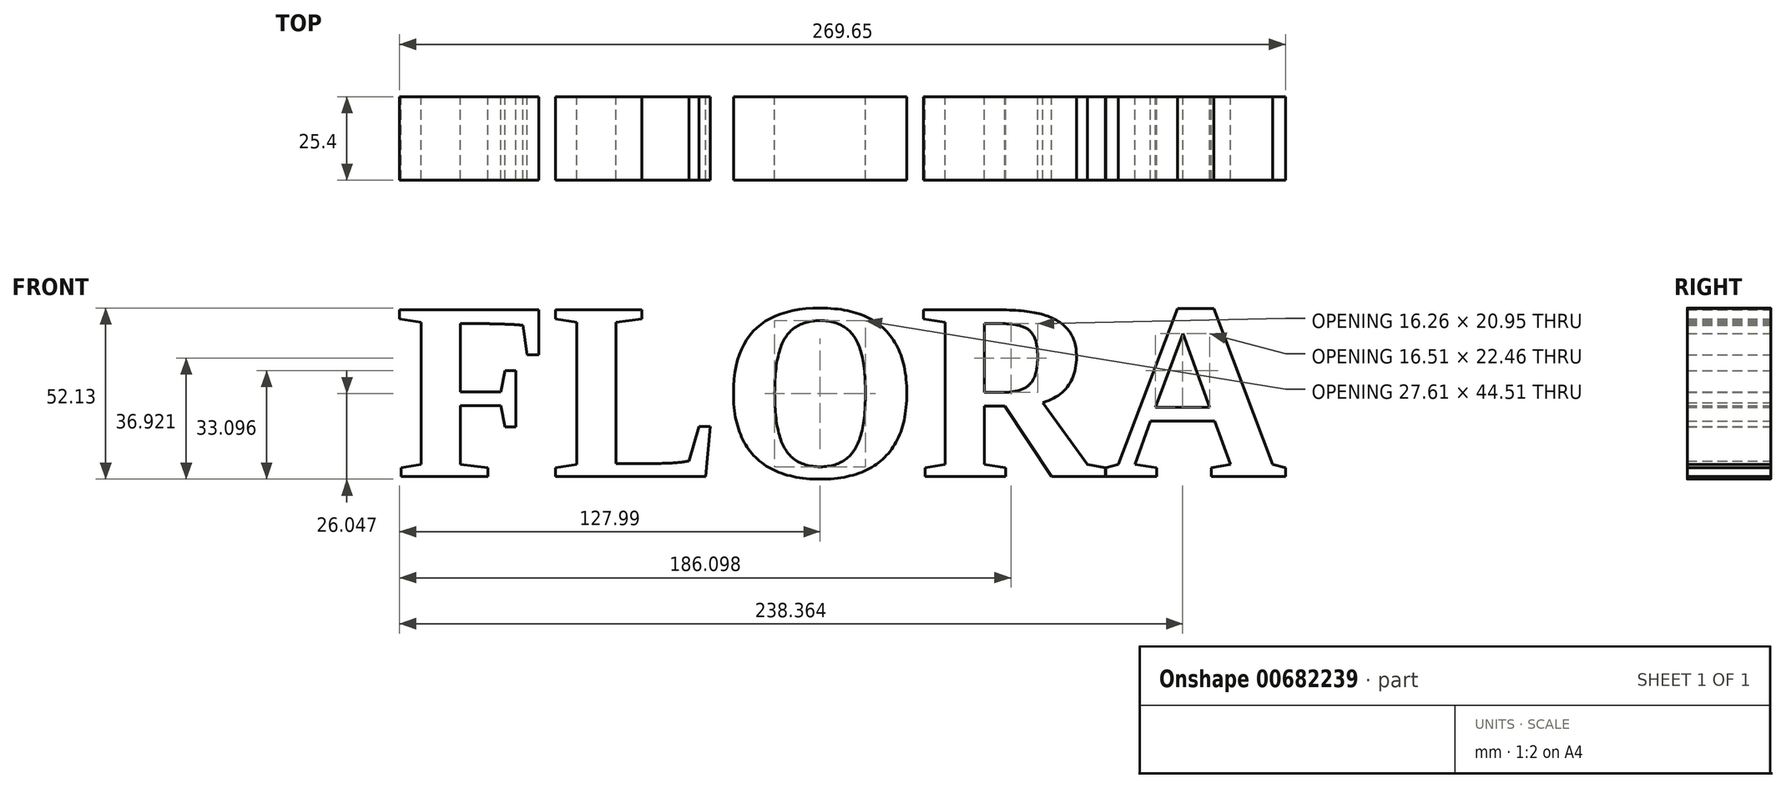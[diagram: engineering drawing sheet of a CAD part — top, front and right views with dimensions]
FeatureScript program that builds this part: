
annotation { "Feature Type Name" : "Feature", "Feature Type Description" : "" }
export const myFeature = defineFeature(function(context is Context, id is Id, definition is map)
    precondition{}
    {
        {
            var Q0;
            Q0=qCreatedBy(makeId("Front.planeOp"),FACE);
            var sketch = newSketch(context, id + "F0", { "sketchPlane" : qUnion([Q0])});
            skText(sketch, "E0", { "text": "FLORA", "fontName": "Tinos-Bold.ttf"});
            const initialGuessF0  = {"E0": [-0.1763, -0.02122, 1, 0, 0.05586]};
            skSetInitialGuess(sketch, initialGuessF0);
            skSolve(sketch);
        }
        {
            var Q0;
            Q0 = qSketchRegion(id + "F0", true);
            extrude(context, id + "F1", {"entities" : qUnion([Q0]), "endBound" : BoundingType.SYMMETRIC, "depth" : 25.4 * mm, "offsetDistance" : 25.4 * mm});
        }
    });
